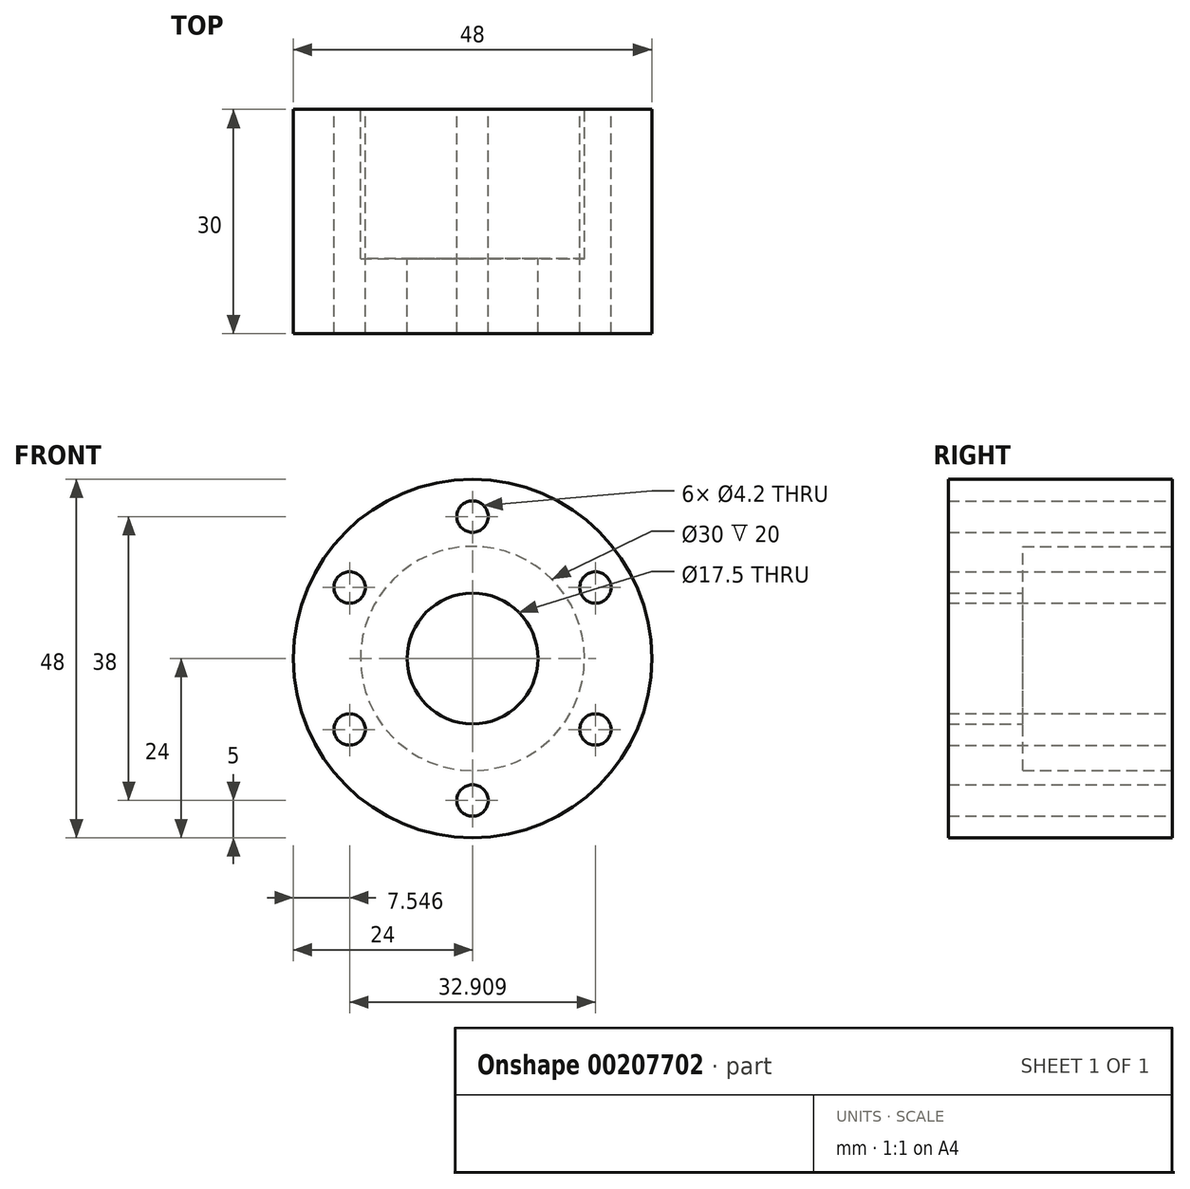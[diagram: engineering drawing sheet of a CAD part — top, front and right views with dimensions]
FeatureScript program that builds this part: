
annotation { "Feature Type Name" : "Feature", "Feature Type Description" : "" }
export const myFeature = defineFeature(function(context is Context, id is Id, definition is map)
    precondition{}
    {
        {
            var Q0;
            Q0=qCreatedBy(makeId("Front.planeOp"),FACE);
            var sketch = newSketch(context, id + "F0", { "sketchPlane" : qUnion([Q0])});
            skCircle(sketch, "E0", {"center": v(0, 0) * mm, "radius": 24 * mm});
            skCircle(sketch, "E1", {"center": v(0, 19) * mm, "radius": 2.1 * mm, "construction": true});
            skCircle(sketch, "E2", {"center": v(0, 0) * mm, "radius": 15 * mm});
            skSolve(sketch);
        }
        {
            var Q0;
            Q0 = qSketchRegion(id + "F0", true);
            extrude(context, id + "F1", {"entities" : qUnion([Q0]), "depth" : 20 * mm});
        }
        {
            var Q0;
            Q0=makeQuery(id+"F1.opExtrude","CAP_FACE",FACE,{"disambiguationData":[OSD([sQuery(id+"F0.wireOp",EDGE,"E0"),sQuery(id+"F0.wireOp",EDGE,"E2")])],"isStart":false});
            var sketch = newSketch(context, id + "F2", { "sketchPlane" : qUnion([Q0])});
            skCircle(sketch, "E3", {"center": v(0, 0) * mm, "radius": 24 * mm});
            skSolve(sketch);
        }
        {
            var Q0;
            Q0 = qSketchRegion(id + "F2", true);
            extrude(context, id + "F3", {"entities" : qUnion([Q0]), "operationType" : NewBodyOperationType.ADD, "depth" : 10 * mm});
        }
        {
            var Q0;
            Q0=makeQuery(id+"F1.opExtrude","CAP_FACE",FACE,{"disambiguationData":[OSD([sQuery(id+"F0.wireOp",EDGE,"E0"),sQuery(id+"F0.wireOp",EDGE,"E2")])],"isStart":true});
            var sketch = newSketch(context, id + "F4", { "sketchPlane" : qUnion([Q0])});
            skCircle(sketch, "E4", {"center": v(0, 19) * mm, "radius": 2.5 * mm});
            skCircle(sketch, "E5.1.0", {"center": v(-16.45, 9.5) * mm, "radius": 2.5 * mm});
            skCircle(sketch, "E5.2.0", {"center": v(-16.45, -9.5) * mm, "radius": 2.5 * mm});
            skCircle(sketch, "E5.3.0", {"center": v(0, -19) * mm, "radius": 2.5 * mm});
            skCircle(sketch, "E5.4.0", {"center": v(16.45, -9.5) * mm, "radius": 2.5 * mm});
            skCircle(sketch, "E5.5.0", {"center": v(16.45, 9.5) * mm, "radius": 2.5 * mm});
            skPoint(sketch, "E5.center", {"position": v(0, 0) * mm});
            skSolve(sketch);
        }
        {
            var Q0;
            Q0=sQuery(id+"F4.wireOp",VERTEX,"E4.center");
            var Q1;
            Q1=sQuery(id+"F4.wireOp",VERTEX,"E5.5.0.center");
            var Q2;
            Q2=sQuery(id+"F4.wireOp",VERTEX,"E5.4.0.center");
            var Q3;
            Q3=sQuery(id+"F4.wireOp",VERTEX,"E5.3.0.center");
            var Q4;
            Q4=sQuery(id+"F4.wireOp",VERTEX,"E5.2.0.center");
            var Q5;
            Q5=sQuery(id+"F4.wireOp",VERTEX,"E5.1.0.center");
            var Q6;
            Q6=makeQuery(id+"F1.opExtrude","SWEPT_BODY",BODY,{"disambiguationData":[OSD([sQuery(id+"F0.wireOp",EDGE,"E0"),sQuery(id+"F0.wireOp",EDGE,"E2")])]});
            hole(context, id + "F5", {"style" : HoleStyle.SIMPLE, "endStyle" : HoleEndStyle.THROUGH, "standardTappedOrClearance" : lookupTablePath({ "standard" : "ISO", "engagement" : "75%", "pitch" : "0.8 mm", "size" : "M5", "type" : "Tapped" }), "standardBlindInLast" : lookupTablePath({ "standard" : "ISO", "engagement" : "75%", "pitch" : "0.8 mm", "size" : "M5", "type" : "Tapped" }), "holeDiameter" : 4.2 * mm, "showTappedDepth" : true, "tappedDepth" : 12 * mm, "tapClearance" : 3, "locations" : qUnion([Q0, Q1, Q2, Q3, Q4, Q5]), "scope" : qUnion([Q6]), "majorDiameter" : 5 * mm});
        }
        {
            var Q0;
            Q0=sQuery(id+"F4.wireOp",VERTEX,"E5.center");
            var Q1;
            Q1=makeQuery(id+"F1.opExtrude","SWEPT_BODY",BODY,{"disambiguationData":[OSD([sQuery(id+"F0.wireOp",EDGE,"E0"),sQuery(id+"F0.wireOp",EDGE,"E2")])]});
            hole(context, id + "F6", {"style" : HoleStyle.SIMPLE, "endStyle" : HoleEndStyle.THROUGH, "standardTappedOrClearance" : lookupTablePath({ "standard" : "ISO", "engagement" : "75%", "pitch" : "2.5 mm", "size" : "M20", "type" : "Tapped" }), "standardBlindInLast" : lookupTablePath({ "standard" : "ISO", "engagement" : "75%", "pitch" : "2.5 mm", "size" : "M20", "type" : "Tapped" }), "holeDiameter" : 17.5 * mm, "showTappedDepth" : true, "tappedDepth" : 12 * mm, "tapClearance" : 3, "locations" : qUnion([Q0]), "scope" : qUnion([Q1]), "majorDiameter" : 20 * mm});
        }
    });
